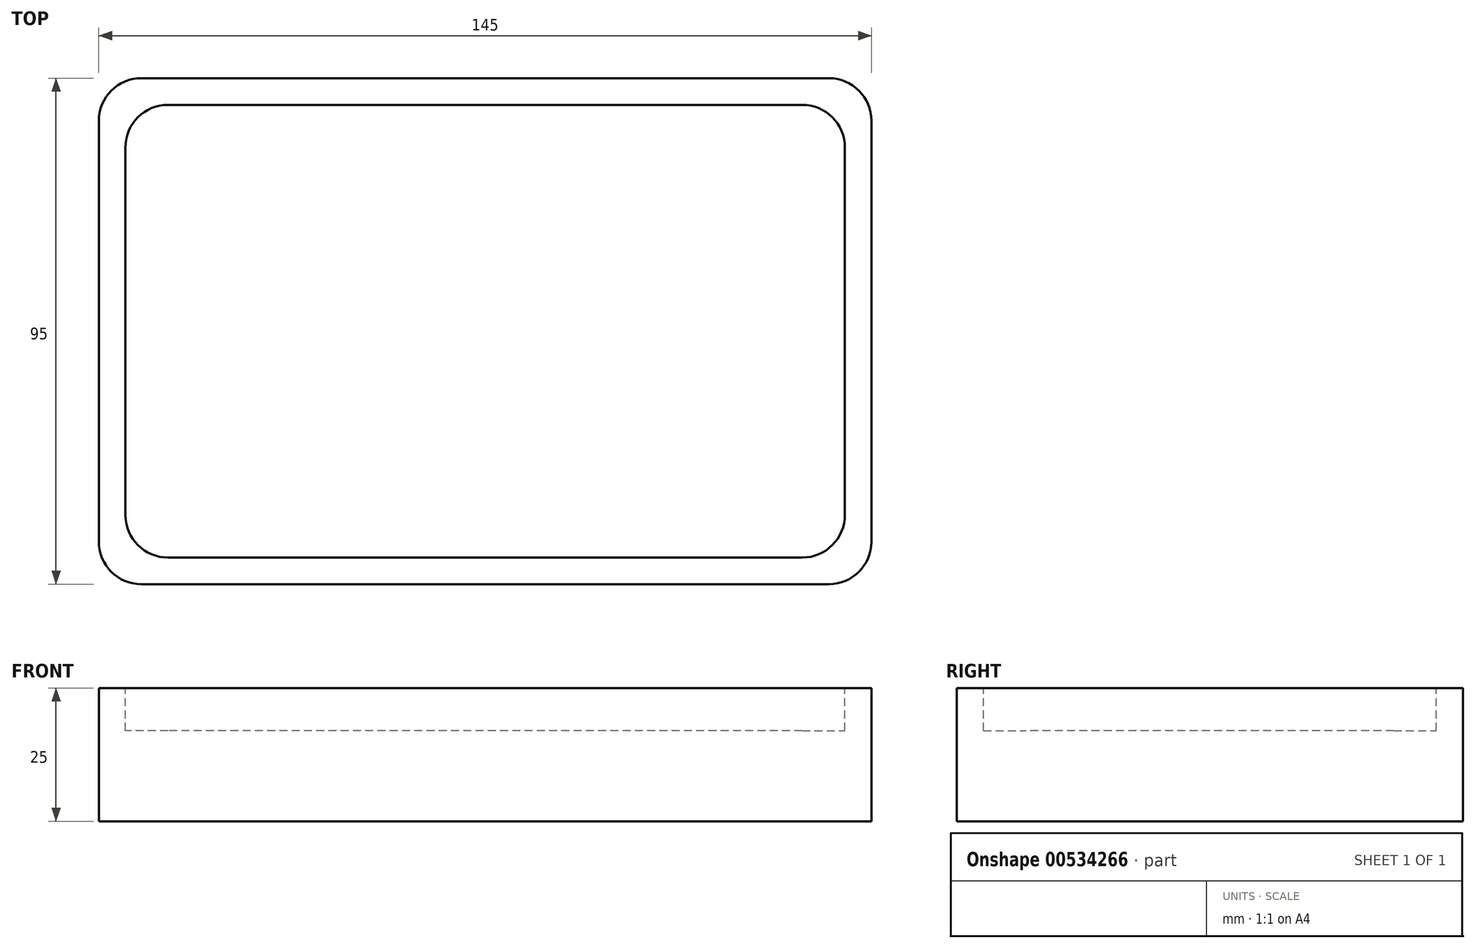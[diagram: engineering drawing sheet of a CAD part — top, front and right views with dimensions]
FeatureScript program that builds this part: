
annotation { "Feature Type Name" : "Feature", "Feature Type Description" : "" }
export const myFeature = defineFeature(function(context is Context, id is Id, definition is map)
    precondition{}
    {
        {
            var Q0;
            Q0=qCreatedBy(makeId("Top.planeOp"),FACE);
            var sketch = newSketch(context, id + "F0", { "sketchPlane" : qUnion([Q0])});
            skLineSegment(sketch, "E0.bottom", {"start": v(-93.83, 83) * mm, "end": v(51.17, 83) * mm});
            skLineSegment(sketch, "E0.top", {"start": v(-93.83, -12) * mm, "end": v(51.17, -12) * mm});
            skLineSegment(sketch, "E0.left", {"start": v(-93.83, 83) * mm, "end": v(-93.83, -12) * mm});
            skLineSegment(sketch, "E0.right", {"start": v(51.17, 83) * mm, "end": v(51.17, -12) * mm});
            skSolve(sketch);
        }
        {
            var Q0;
            Q0=makeQuery(id+"F0.imprint","IMPRINT",FACE,{"disambiguationData":[TD([[makeQuery(id+"F0.imprint","IMPRINT",EDGE,{"derivedFrom":sQuery(id+"F0.wireOp",EDGE,"E0.bottom")}),-1.0]])]});
            extrude(context, id + "F1", {"entities" : qUnion([Q0]), "depth" : 25 * mm, "offsetDistance" : 25 * mm});
        }
        {
            var Q0;
            Q0=makeQuery(id+"F1.opExtrude","SWEPT_EDGE",EDGE,{"disambiguationData":[OSD([sQuery(id+"F0.wireOp",EDGE,"E0.top"),sQuery(id+"F0.wireOp",EDGE,"E0.left")])]});
            var Q1;
            Q1=makeQuery(id+"F1.opExtrude","SWEPT_EDGE",EDGE,{"disambiguationData":[OSD([sQuery(id+"F0.wireOp",EDGE,"E0.top"),sQuery(id+"F0.wireOp",EDGE,"E0.right")])]});
            var Q2;
            Q2=makeQuery(id+"F1.opExtrude","SWEPT_EDGE",EDGE,{"disambiguationData":[OSD([sQuery(id+"F0.wireOp",EDGE,"E0.bottom"),sQuery(id+"F0.wireOp",EDGE,"E0.right")])]});
            var Q3;
            Q3=makeQuery(id+"F1.opExtrude","SWEPT_EDGE",EDGE,{"disambiguationData":[OSD([sQuery(id+"F0.wireOp",EDGE,"E0.bottom"),sQuery(id+"F0.wireOp",EDGE,"E0.left")])]});
            fillet(context, id + "F2", {"entities" : qUnion([Q0, Q1, Q2, Q3]), "radius" : 8 * mm, "tangentPropagation" : true, "allowEdgeOverflow" : false});
        }
        {
            var Q0;
            Q0=makeQuery(id+"F1.opExtrude","CAP_FACE",FACE,{"disambiguationData":[OSD([sQuery(id+"F0.wireOp",EDGE,"E0.bottom"),sQuery(id+"F0.wireOp",EDGE,"E0.top"),sQuery(id+"F0.wireOp",EDGE,"E0.left"),sQuery(id+"F0.wireOp",EDGE,"E0.right")])],"isStart":false});
            var sketch = newSketch(context, id + "F3", { "sketchPlane" : qUnion([Q0])});
            skLineSegment(sketch, "E1.0", {"start": v(-88.83, 78) * mm, "end": v(-88.83, -7) * mm});
            skLineSegment(sketch, "E1.1", {"start": v(46.17, 78) * mm, "end": v(-88.83, 78) * mm});
            skLineSegment(sketch, "E1.2", {"start": v(46.17, -7) * mm, "end": v(46.17, 78) * mm});
            skLineSegment(sketch, "E1.3", {"start": v(-88.83, -7) * mm, "end": v(46.17, -7) * mm});
            skSolve(sketch);
        }
        {
            var Q0;
            Q0=makeQuery(id+"F3.imprint","IMPRINT",FACE,{"disambiguationData":[TD([[makeQuery(id+"F3.imprint","IMPRINT",EDGE,{"derivedFrom":sQuery(id+"F3.wireOp",EDGE,"E1.0")}),1.0]])]});
            extrude(context, id + "F4", {"entities" : qUnion([Q0]), "operationType" : NewBodyOperationType.REMOVE, "oppositeDirection" : true, "depth" : 8 * mm, "offsetDistance" : 25 * mm});
        }
        {
            var Q0;
            Q0=makeQuery(id+"F4.boolean.opBoolean","COPY",EDGE,{"derivedFrom":makeQuery(id+"F4.opExtrude","SWEPT_EDGE",EDGE,{"disambiguationData":[OSD([sQuery(id+"F3.wireOp",EDGE,"E1.0"),sQuery(id+"F3.wireOp",EDGE,"E1.1")])]})});
            var Q1;
            Q1=makeQuery(id+"F4.boolean.opBoolean","COPY",EDGE,{"derivedFrom":makeQuery(id+"F4.opExtrude","SWEPT_EDGE",EDGE,{"disambiguationData":[OSD([sQuery(id+"F3.wireOp",EDGE,"E1.0"),sQuery(id+"F3.wireOp",EDGE,"E1.3")])]})});
            var Q2;
            Q2=makeQuery(id+"F4.boolean.opBoolean","COPY",EDGE,{"derivedFrom":makeQuery(id+"F4.opExtrude","SWEPT_EDGE",EDGE,{"disambiguationData":[OSD([sQuery(id+"F3.wireOp",EDGE,"E1.1"),sQuery(id+"F3.wireOp",EDGE,"E1.2")])]})});
            var Q3;
            Q3=makeQuery(id+"F4.boolean.opBoolean","COPY",EDGE,{"derivedFrom":makeQuery(id+"F4.opExtrude","SWEPT_EDGE",EDGE,{"disambiguationData":[OSD([sQuery(id+"F3.wireOp",EDGE,"E1.2"),sQuery(id+"F3.wireOp",EDGE,"E1.3")])]})});
            fillet(context, id + "F5", {"entities" : qUnion([Q0, Q1, Q2, Q3]), "radius" : 8 * mm, "tangentPropagation" : true, "allowEdgeOverflow" : false});
        }
    });
